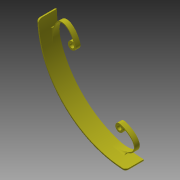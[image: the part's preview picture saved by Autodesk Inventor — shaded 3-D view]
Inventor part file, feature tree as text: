
AUTODESK INVENTOR PART (.ipt)
format: ipt  version: 2015 (Build 190159000, 159)  size: 253,440 bytes
history: native  units: mm
features: extrude x4, sketch x4, fillet x4, other x1
ambient origin geometry x8: Origin, YZ Plane, XZ Plane, XY Plane, X Axis, Y Axis, Z Axis, Center Point
bodies: Body1 (feature_tree)
feature tree (13):
  other  "Sólido1"
  extrude  "Extrusión1"  Depth=300.0mm
  sketch  "Boceto3"  dims[d2=270.0mm d3=10.0mm]
  extrude  "Extrusión3"  Depth=10.0mm
  extrude  "Extrusión4"  Depth=3.0mm
  extrude  "Extrusión5"  Depth=3.0mm
  fillet  "Empalme2"  Radius=3.0mm
  fillet  "Empalme3"  Radius=0.5mm
  fillet  "Empalme4"  Radius=6.0mm
  fillet  "Empalme5"  Radius=35.0mm
  sketch  "Boceto1"  dims[d0=292.0mm d1=300.0mm]
  sketch  "Boceto4"  dims[d4=6.0mm d6=3.0mm]
  sketch  "Boceto5"  dims[d7=0.5mm d8=35.0mm d9=3.0mm d10=0.5mm d11=6.0mm d12=35.0mm d14=8.0mm d15=0.0mm d19=1.5mm d20=1.5mm d23=135.0deg d27=0.174533mm d28=0.174533mm d29=8.0mm d30=0.0mm d31=8.0mm d32=0.0mm d33=30.0mm d34=0.0mm d35=1.0mm d36=5.0mm d37=5.0mm d38=3.0mm]
